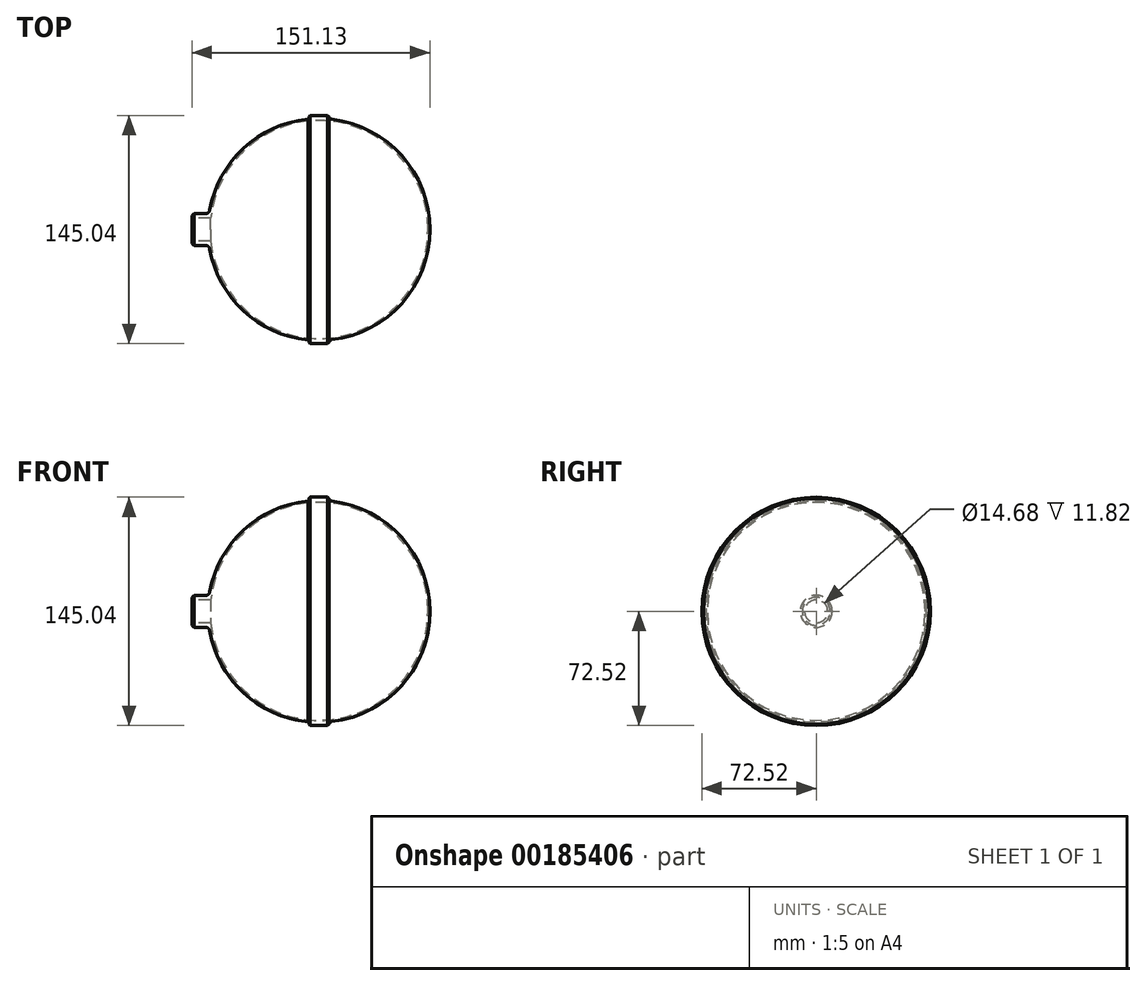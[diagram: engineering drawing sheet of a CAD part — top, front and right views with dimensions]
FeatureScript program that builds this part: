
annotation { "Feature Type Name" : "Feature", "Feature Type Description" : "" }
export const myFeature = defineFeature(function(context is Context, id is Id, definition is map)
    precondition{}
    {
        {
            var Q0;
            Q0=qCreatedBy(makeId("Front.planeOp"),FACE);
            var sketch = newSketch(context, id + "F0", { "sketchPlane" : qUnion([Q0])});
            skArc(sketch, "E0", {"start": v(-69.22, 0) * mm, "mid": v(0, -69.22) * mm, "end": v(69.22, 0) * mm});
            skArc(sketch, "E1", {"start": v(-70.48, 0) * mm, "mid": v(0, -70.48) * mm, "end": v(70.48, 0) * mm});
            skLineSegment(sketch, "E2", {"start": v(0, 0) * mm, "end": v(-70.49, 0) * mm});
            skLineSegment(sketch, "E3", {"start": v(-80.65, 0) * mm, "end": v(-80.65, -10.16) * mm});
            skLineSegment(sketch, "E4", {"start": v(-80.65, -10.16) * mm, "end": v(-69.75, -10.16) * mm});
            skLineSegment(sketch, "E5", {"start": v(-70.49, 0) * mm, "end": v(-80.65, 0) * mm});
            skPoint(sketch, "E6.orphan", {"position": v(-80.65, 10.16) * mm});
            skLineSegment(sketch, "E7", {"start": v(0, 0) * mm, "end": v(70.49, 0) * mm});
            skLineSegment(sketch, "E8", {"start": v(0, -70.48) * mm, "end": v(0, -72.52) * mm});
            skLineSegment(sketch, "E9", {"start": v(0, -72.52) * mm, "end": v(-6.35, -72.52) * mm});
            skLineSegment(sketch, "E10", {"start": v(-6.35, -72.52) * mm, "end": v(6.35, -72.52) * mm});
            skLineSegment(sketch, "E11", {"start": v(6.35, -72.52) * mm, "end": v(6.35, -70.2) * mm});
            skLineSegment(sketch, "E12", {"start": v(-6.35, -72.52) * mm, "end": v(-6.35, -70.2) * mm});
            skSolve(sketch);
        }
        {
            var Q0;
            Q0=makeQuery(id+"F0.imprint","IMPRINT",FACE,{"disambiguationData":[TD([[makeQuery(id+"F0.imprint","IMPRINT",EDGE,{"derivedFrom":sQuery(id+"F0.wireOp",EDGE,"E3")}),1.0]])]});
            var Q1;
            {var subQ1=sQuery(id+"F0.wireOp",EDGE,"E0");Q1=makeQuery(id+"F0.imprint","IMPRINT",FACE,{"disambiguationData":[TD([[makeQuery(id+"F0.imprint","IMPRINT",EDGE,{"derivedFrom":subQ1}),-1.0]])]});}
            var Q2;
            {var subQ0=sQuery(id+"F0.wireOp",EDGE,"E8");Q2=makeQuery(id+"F0.imprint","IMPRINT",FACE,{"disambiguationData":[TD([[makeQuery(id+"F0.imprint","IMPRINT",EDGE,{"derivedFrom":subQ0}),-1.0]])]});}
            var Q3;
            {var subQ0=sQuery(id+"F0.wireOp",EDGE,"E8");Q3=makeQuery(id+"F0.imprint","IMPRINT",FACE,{"disambiguationData":[TD([[makeQuery(id+"F0.imprint","IMPRINT",EDGE,{"derivedFrom":subQ0}),1.0]])]});}
            var Q4;
            Q4=sQuery(id+"F0.wireOp",EDGE,"E2");
            revolve(context, id + "F1", {"entities" : qUnion([Q0, Q1, Q2, Q3]), "axis" : qUnion([Q4]), "revolveType" : RevolveType.FULL});
        }
        {
            var Q0;
            Q0=makeQuery(id+"F1.opRevolve","SWEPT_EDGE",EDGE,{"disambiguationData":[OSD([sQuery(id+"F0.wireOp",EDGE,"E1"),sQuery(id+"F0.wireOp",EDGE,"E4")])]});
            fillet(context, id + "F2", {"entities" : qUnion([Q0]), "radius" : 2.54 * mm, "tangentPropagation" : true, "allowEdgeOverflow" : false});
        }
        {
            var Q0;
            Q0=makeQuery(id+"F1.opRevolve","SWEPT_FACE",FACE,{"disambiguationData":[OSD([sQuery(id+"F0.wireOp",EDGE,"E3")])]});
            var sketch = newSketch(context, id + "F3", { "sketchPlane" : qUnion([Q0])});
            skCircle(sketch, "E13", {"center": v(0, 0) * mm, "radius": 7.34 * mm});
            skSolve(sketch);
        }
        {
            var Q0;
            Q0=sQuery(id+"F3.wireOp",VERTEX,"E13.center");
            var Q1;
            Q1=makeQuery(id+"F1.opRevolve","SWEPT_BODY",BODY,{"disambiguationData":[OSD([sQuery(id+"F0.wireOp",EDGE,"E0"),sQuery(id+"F0.wireOp",EDGE,"E1"),sQuery(id+"F0.wireOp",EDGE,"E2"),sQuery(id+"F0.wireOp",EDGE,"E3"),sQuery(id+"F0.wireOp",EDGE,"E4"),sQuery(id+"F0.wireOp",EDGE,"E5"),sQuery(id+"F0.wireOp",EDGE,"E7")])]});
            hole(context, id + "F4", {"style" : HoleStyle.SIMPLE, "endStyle" : HoleEndStyle.BLIND, "holeDiameter" : 14.68 * mm, "holeDepth" : 12.7 * mm, "locations" : qUnion([Q0]), "scope" : qUnion([Q1])});
        }
        {
            var Q0;
            Q0=makeQuery(id+"F1.opRevolve","SWEPT_EDGE",EDGE,{"disambiguationData":[OSD([sQuery(id+"F0.wireOp",EDGE,"E3"),sQuery(id+"F0.wireOp",EDGE,"E4")])]});
            chamfer(context, id + "F5", {"entities" : qUnion([Q0]), "width" : 1.27 * mm, "tangentPropagation" : true});
        }
        {
            var Q0;
            Q0=makeQuery(id+"F1.opRevolve","SWEPT_EDGE",EDGE,{"disambiguationData":[OSD([sQuery(id+"F0.wireOp",EDGE,"E10"),sQuery(id+"F0.wireOp",EDGE,"E12")])]});
            var Q1;
            Q1=makeQuery(id+"F1.opRevolve","SWEPT_EDGE",EDGE,{"disambiguationData":[OSD([sQuery(id+"F0.wireOp",EDGE,"E10"),sQuery(id+"F0.wireOp",EDGE,"E11")])]});
            chamfer(context, id + "F6", {"entities" : qUnion([Q0, Q1]), "width" : 0.76 * mm, "tangentPropagation" : true});
        }
        {
            var Q0;
            Q0=makeQuery(id+"F1.opRevolve","SWEPT_EDGE",EDGE,{"disambiguationData":[OSD([sQuery(id+"F0.wireOp",EDGE,"E1"),sQuery(id+"F0.wireOp",EDGE,"E12")])]});
            var Q1;
            Q1=makeQuery(id+"F1.opRevolve","SWEPT_EDGE",EDGE,{"disambiguationData":[OSD([sQuery(id+"F0.wireOp",EDGE,"E1"),sQuery(id+"F0.wireOp",EDGE,"E11")])]});
            fillet(context, id + "F7", {"entities" : qUnion([Q0, Q1]), "radius" : 2.03 * mm, "tangentPropagation" : true, "allowEdgeOverflow" : false});
        }
    });
